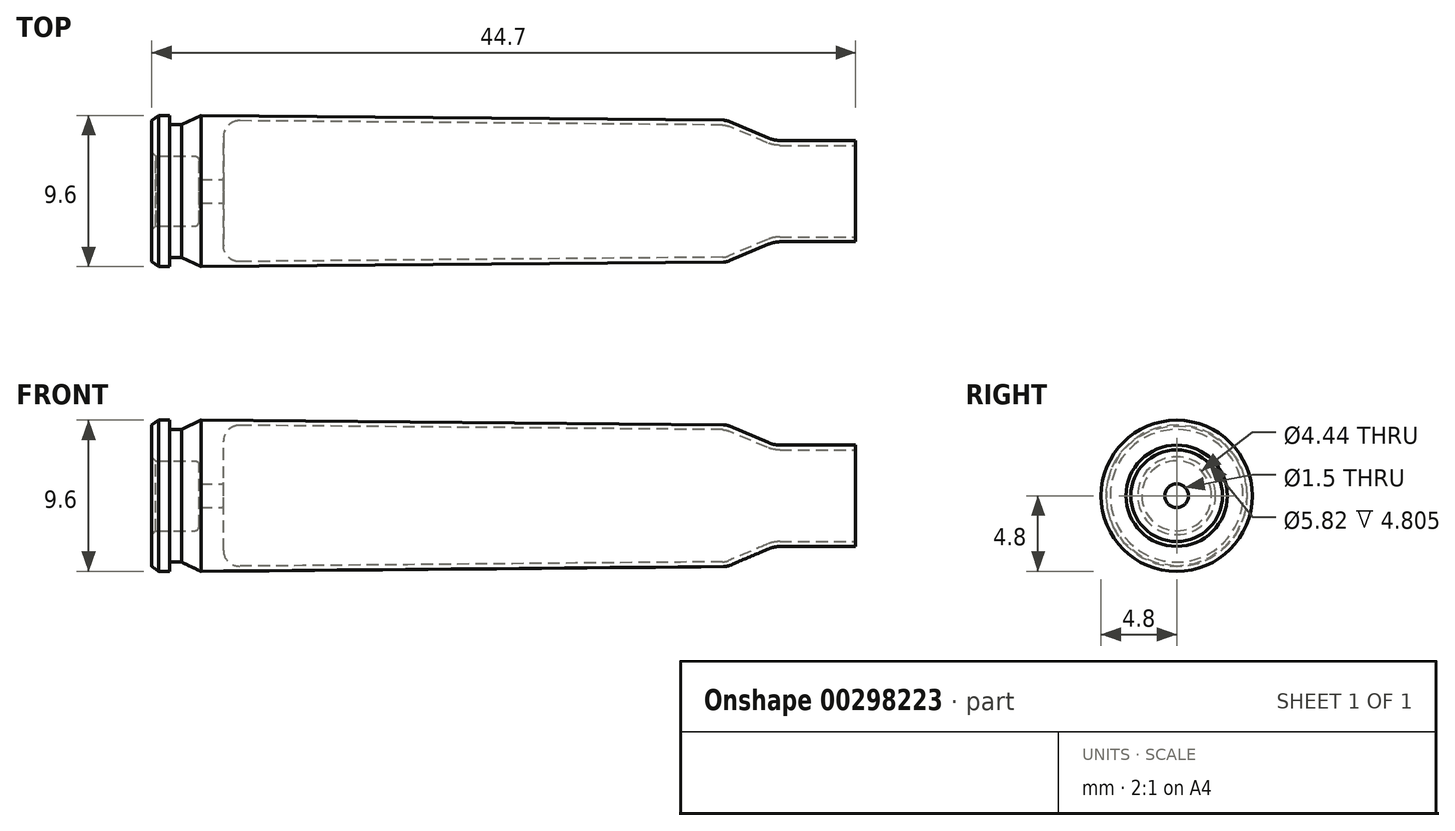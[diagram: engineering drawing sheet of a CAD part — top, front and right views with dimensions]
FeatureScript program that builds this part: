
annotation { "Feature Type Name" : "Feature", "Feature Type Description" : "" }
export const myFeature = defineFeature(function(context is Context, id is Id, definition is map)
    precondition{}
    {
        {
            var Q0;
            Q0=qCreatedBy(makeId("Top.planeOp"),FACE);
            var sketch = newSketch(context, id + "F0", { "sketchPlane" : qUnion([Q0])});
            skLineSegment(sketch, "E0", {"start": v(0, 2.22) * mm, "end": v(0, 4.48) * mm});
            skLineSegment(sketch, "E1", {"start": v(0, 4.48) * mm, "end": v(0.45, 4.8) * mm});
            skLineSegment(sketch, "E2", {"start": v(0.45, 4.8) * mm, "end": v(1.14, 4.8) * mm});
            skLineSegment(sketch, "E3", {"start": v(1.14, 4.8) * mm, "end": v(1.14, 4.22) * mm});
            skLineSegment(sketch, "E4", {"start": v(1.14, 4.22) * mm, "end": v(1.9, 4.22) * mm});
            skLineSegment(sketch, "E5", {"start": v(1.9, 4.22) * mm, "end": v(3.13, 4.8) * mm});
            skLineSegment(sketch, "E6", {"start": v(3.13, 4.8) * mm, "end": v(36.32, 4.5) * mm});
            skLineSegment(sketch, "E7", {"start": v(44.7, 0) * mm, "end": v(0, 0) * mm});
            skLineSegment(sketch, "E8", {"start": v(39.96, 3.21) * mm, "end": v(44.7, 3.21) * mm});
            skLineSegment(sketch, "E9", {"start": v(44.7, 3.21) * mm, "end": v(44.7, 2.91) * mm});
            skLineSegment(sketch, "E10", {"start": v(36.7, 4.42) * mm, "end": v(39.18, 3.37) * mm});
            skLineSegment(sketch, "E11.0", {"start": v(39.9, 2.91) * mm, "end": v(44.7, 2.91) * mm});
            skLineSegment(sketch, "E11.1", {"start": v(36.64, 4.12) * mm, "end": v(39.11, 3.07) * mm});
            skLineSegment(sketch, "E11.2", {"start": v(5.57, 4.47) * mm, "end": v(36.26, 4.2) * mm});
            skLineSegment(sketch, "E12", {"start": v(4.56, 3.47) * mm, "end": v(4.56, 0.85) * mm});
            skPoint(sketch, "E13.visualSharp", {"position": v(4.56, 4.48) * mm});
            skArc(sketch, "E13.filletArc", {"start": v(5.57, 4.47) * mm, "mid": v(4.86, 4.18) * mm, "end": v(4.56, 3.47) * mm});
            skPoint(sketch, "E14.visualSharp", {"position": v(36.52, 4.5) * mm});
            skArc(sketch, "E14.filletArc", {"start": v(36.7, 4.42) * mm, "mid": v(36.52, 4.48) * mm, "end": v(36.32, 4.5) * mm});
            skPoint(sketch, "E15.visualSharp", {"position": v(39.55, 3.21) * mm});
            skArc(sketch, "E15.filletArc", {"start": v(39.18, 3.37) * mm, "mid": v(39.56, 3.26) * mm, "end": v(39.96, 3.21) * mm});
            skPoint(sketch, "E16.visualSharp", {"position": v(39.49, 2.91) * mm});
            skArc(sketch, "E16.filletArc", {"start": v(39.11, 3.07) * mm, "mid": v(39.5, 2.95) * mm, "end": v(39.9, 2.91) * mm});
            skPoint(sketch, "E17.visualSharp", {"position": v(36.46, 4.2) * mm});
            skArc(sketch, "E17.filletArc", {"start": v(36.64, 4.12) * mm, "mid": v(36.45, 4.18) * mm, "end": v(36.26, 4.2) * mm});
            skLineSegment(sketch, "E18", {"start": v(0, 2.22) * mm, "end": v(2.75, 2.22) * mm});
            skLineSegment(sketch, "E19", {"start": v(3, 1.97) * mm, "end": v(3, 0.85) * mm});
            skLineSegment(sketch, "E20", {"start": v(3.1, 0.75) * mm, "end": v(4.46, 0.75) * mm});
            skPoint(sketch, "E21.visualSharp", {"position": v(3, 2.22) * mm});
            skArc(sketch, "E21.filletArc", {"start": v(3, 1.97) * mm, "mid": v(2.93, 2.15) * mm, "end": v(2.75, 2.22) * mm});
            skPoint(sketch, "E22.visualSharp", {"position": v(3, 0.75) * mm});
            skArc(sketch, "E22.filletArc", {"start": v(3, 0.85) * mm, "mid": v(3.03, 0.78) * mm, "end": v(3.1, 0.75) * mm});
            skPoint(sketch, "E23.newPointA", {"position": v(4.56, 0) * mm});
            skArc(sketch, "E23.filletArc", {"start": v(4.46, 0.75) * mm, "mid": v(4.53, 0.78) * mm, "end": v(4.56, 0.85) * mm});
            skSolve(sketch);
        }
        {
            var Q0;
            Q0=makeQuery(id+"F0.imprint","IMPRINT",FACE,{"disambiguationData":[TD([[makeQuery(id+"F0.imprint","IMPRINT",EDGE,{"derivedFrom":sQuery(id+"F0.wireOp",EDGE,"E0")}),-1.0]])]});
            var Q1;
            Q1=sQuery(id+"F0.wireOp",EDGE,"E7");
            revolve(context, id + "F1", {"entities" : qUnion([Q0]), "axis" : qUnion([Q1]), "revolveType" : RevolveType.FULL});
        }
        {
            var Q0;
            Q0=makeQuery(id+"F1.opRevolve","SWEPT_EDGE",EDGE,{"disambiguationData":[OSD([sQuery(id+"F0.wireOp",EDGE,"E0"),sQuery(id+"F0.wireOp",EDGE,"E18")])]});
            chamfer(context, id + "F2", {"entities" : qUnion([Q0]), "width" : .25 * mm, "tangentPropagation" : true});
        }
    });
